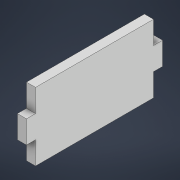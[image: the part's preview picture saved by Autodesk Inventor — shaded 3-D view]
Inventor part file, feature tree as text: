
AUTODESK INVENTOR PART (.ipt)
format: ipt  version: 2022 (Build 260153000, 153)  size: 101,888 bytes
history: native  units: mm
features: other x1, extrude x1, sketch x1
ambient origin geometry x8: Origin, YZ Plane, XZ Plane, XY Plane, X Axis, Y Axis, Z Axis, Center Point
bodies: Body1 (feature_tree)
feature tree (3):
  other  "Твердое тело1"
  extrude  "Выдавливание1"  Depth=30.0mm
  sketch  "Эскиз1"
